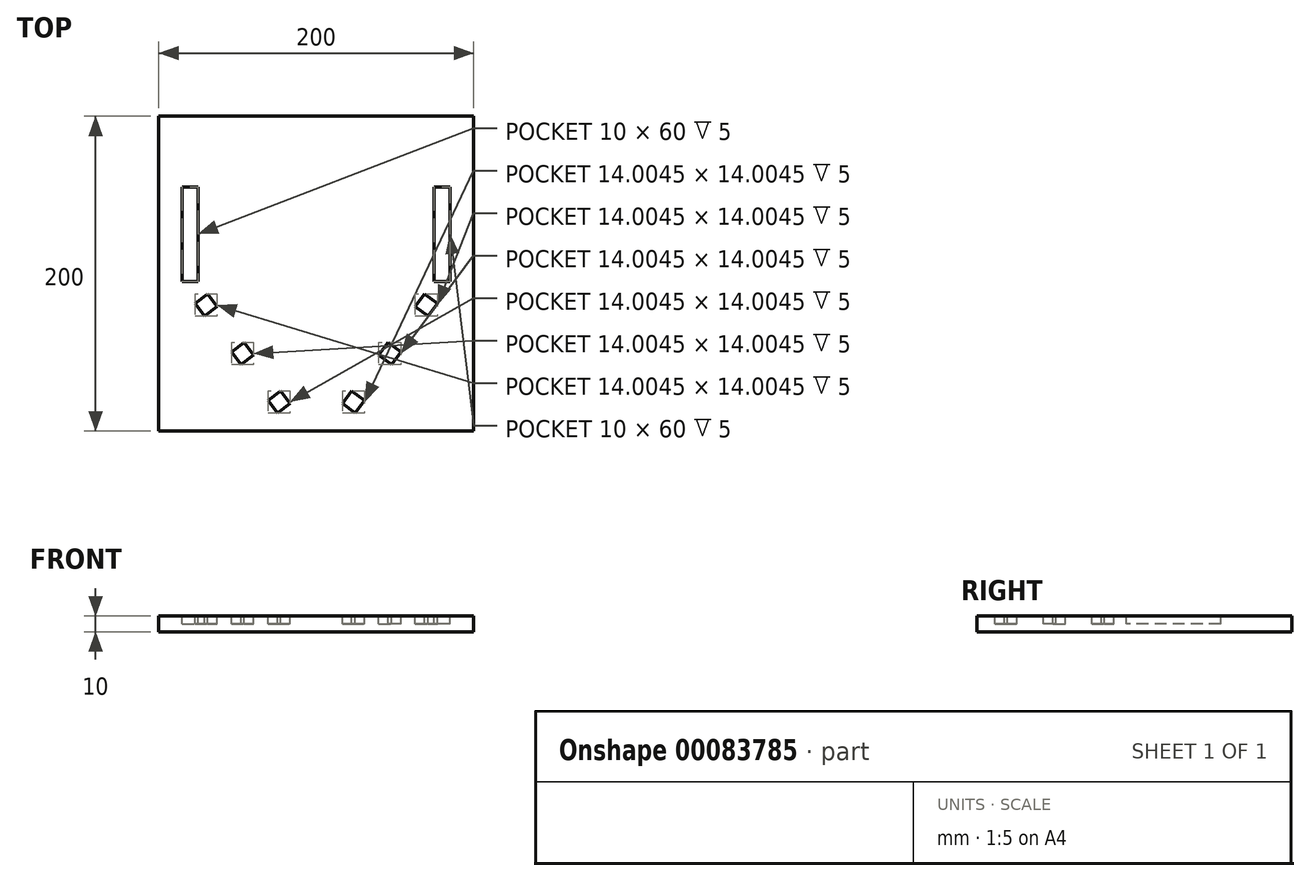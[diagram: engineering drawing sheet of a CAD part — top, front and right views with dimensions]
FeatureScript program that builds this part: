
annotation { "Feature Type Name" : "Feature", "Feature Type Description" : "" }
export const myFeature = defineFeature(function(context is Context, id is Id, definition is map)
    precondition{}
    {
        {
            var Q0;
            Q0=qCreatedBy(makeId("Top.planeOp"),FACE);
            var sketch = newSketch(context, id + "F0", { "sketchPlane" : qUnion([Q0])});
            skLineSegment(sketch, "E0.bottom", {"start": v(-100, 100) * mm, "end": v(100, 100) * mm});
            skLineSegment(sketch, "E0.top", {"start": v(-100, -100) * mm, "end": v(100, -100) * mm});
            skLineSegment(sketch, "E0.left", {"start": v(-100, 100) * mm, "end": v(-100, -100) * mm});
            skLineSegment(sketch, "E0.right", {"start": v(100, 100) * mm, "end": v(100, -100) * mm});
            skPoint(sketch, "E0.middle", {"position": v(0, 0) * mm});
            skSolve(sketch);
        }
        {
            var Q0;
            Q0=makeQuery(id+"F0.imprint","IMPRINT",FACE,{"disambiguationData":[TD([[makeQuery(id+"F0.imprint","IMPRINT",EDGE,{"derivedFrom":sQuery(id+"F0.wireOp",EDGE,"E0.bottom")}),-1.0]])]});
            extrude(context, id + "F1", {"entities" : qUnion([Q0]), "depth" : 10 * mm});
        }
        {
            var Q0;
            Q0=makeQuery(id+"F1.opExtrude","CAP_FACE",FACE,{"disambiguationData":[OSD([sQuery(id+"F0.wireOp",EDGE,"E0.bottom"),sQuery(id+"F0.wireOp",EDGE,"E0.top"),sQuery(id+"F0.wireOp",EDGE,"E0.left"),sQuery(id+"F0.wireOp",EDGE,"E0.right")])],"isStart":false});
            var sketch = newSketch(context, id + "F2", { "sketchPlane" : qUnion([Q0])});
            skLineSegment(sketch, "E1", {"start": v(-100, 25) * mm, "end": v(100, 25) * mm, "construction": true});
            skLineSegment(sketch, "E2.bottom", {"start": v(-85, 55) * mm, "end": v(-75, 55) * mm});
            skLineSegment(sketch, "E2.top", {"start": v(-85, -5) * mm, "end": v(-75, -5) * mm});
            skLineSegment(sketch, "E2.left", {"start": v(-85, 55) * mm, "end": v(-85, -5) * mm});
            skLineSegment(sketch, "E2.right", {"start": v(-75, 55) * mm, "end": v(-75, -5) * mm});
            skPoint(sketch, "E2.middle", {"position": v(-80, 25) * mm});
            skLineSegment(sketch, "E3", {"start": v(0, 100) * mm, "end": v(0, -100) * mm, "construction": true});
            skLineSegment(sketch, "E4.MirrorCS", {"start": v(85, 55) * mm, "end": v(75, 55) * mm});
            skLineSegment(sketch, "E5.MirrorCS", {"start": v(85, -5) * mm, "end": v(75, -5) * mm});
            skLineSegment(sketch, "E6.MirrorCS", {"start": v(75, 55) * mm, "end": v(75, -5) * mm});
            skLineSegment(sketch, "E7.MirrorCS", {"start": v(85, 55) * mm, "end": v(85, -5) * mm});
            skPoint(sketch, "E8.MirrorP", {"position": v(80, 25) * mm});
            skLineSegment(sketch, "E9", {"start": v(-75, -5) * mm, "end": v(-10.6, -90.45) * mm, "construction": true});
            skLineSegment(sketch, "E10", {"start": v(-10.6, -90.45) * mm, "end": v(-18.6, -96.47) * mm, "construction": true});
            skLineSegment(sketch, "E11", {"start": v(-18.6, -96.47) * mm, "end": v(-82.99, -11.02) * mm, "construction": true});
            skLineSegment(sketch, "E12", {"start": v(-82.99, -11.02) * mm, "end": v(-75, -5) * mm, "construction": true});
            skLineSegment(sketch, "E13.MirrorCS", {"start": v(82.99, -11.02) * mm, "end": v(75, -5) * mm, "construction": true});
            skLineSegment(sketch, "E14.MirrorCS", {"start": v(10.6, -90.45) * mm, "end": v(18.6, -96.47) * mm, "construction": true});
            skLineSegment(sketch, "E15.MirrorCS", {"start": v(18.6, -96.47) * mm, "end": v(82.99, -11.02) * mm, "construction": true});
            skLineSegment(sketch, "E16.MirrorCS", {"start": v(75, -5) * mm, "end": v(10.6, -90.45) * mm, "construction": true});
            skLineSegment(sketch, "E17", {"start": v(-76.97, -19) * mm, "end": v(-68.98, -12.99) * mm});
            skLineSegment(sketch, "E18", {"start": v(-68.98, -12.99) * mm, "end": v(-62.96, -20.97) * mm});
            skLineSegment(sketch, "E19", {"start": v(-62.96, -20.97) * mm, "end": v(-70.95, -27) * mm});
            skLineSegment(sketch, "E20", {"start": v(-70.95, -27) * mm, "end": v(-76.97, -19) * mm});
            skLineSegment(sketch, "E21", {"start": v(-42.8, -47.73) * mm, "end": v(-50.79, -53.75) * mm, "construction": true});
            skLineSegment(sketch, "E22", {"start": v(-53.8, -49.75) * mm, "end": v(-45.81, -43.73) * mm});
            skLineSegment(sketch, "E23", {"start": v(-45.81, -43.73) * mm, "end": v(-39.8, -51.72) * mm});
            skLineSegment(sketch, "E24", {"start": v(-39.8, -51.72) * mm, "end": v(-47.78, -57.74) * mm});
            skLineSegment(sketch, "E25", {"start": v(-47.78, -57.74) * mm, "end": v(-53.8, -49.75) * mm});
            skLineSegment(sketch, "E26.MirrorCS", {"start": v(-30.63, -80.5) * mm, "end": v(-24.61, -88.49) * mm});
            skLineSegment(sketch, "E27.MirrorCS", {"start": v(-24.61, -88.49) * mm, "end": v(-16.62, -82.47) * mm});
            skLineSegment(sketch, "E28.MirrorCS", {"start": v(-16.62, -82.47) * mm, "end": v(-22.64, -74.48) * mm});
            skLineSegment(sketch, "E29.MirrorCS", {"start": v(-22.64, -74.48) * mm, "end": v(-30.63, -80.5) * mm});
            skLineSegment(sketch, "E30.MirrorCS", {"start": v(-39.8, -51.72) * mm, "end": v(-45.81, -43.73) * mm});
            skLineSegment(sketch, "E31.MirrorCS", {"start": v(-53.8, -49.75) * mm, "end": v(-47.78, -57.74) * mm});
            skLineSegment(sketch, "E32.MirrorCS", {"start": v(-45.81, -43.73) * mm, "end": v(-53.8, -49.75) * mm});
            skLineSegment(sketch, "E33.MirrorCS", {"start": v(-47.78, -57.74) * mm, "end": v(-39.8, -51.72) * mm});
            skLineSegment(sketch, "E34.MirrorCS", {"start": v(16.62, -82.47) * mm, "end": v(22.64, -74.48) * mm});
            skLineSegment(sketch, "E35.MirrorCS", {"start": v(68.98, -12.99) * mm, "end": v(62.96, -20.97) * mm});
            skLineSegment(sketch, "E36.MirrorCS", {"start": v(70.95, -27) * mm, "end": v(76.97, -19) * mm});
            skLineSegment(sketch, "E37.MirrorCS", {"start": v(53.8, -49.75) * mm, "end": v(47.78, -57.74) * mm});
            skLineSegment(sketch, "E38.MirrorCS", {"start": v(39.8, -51.72) * mm, "end": v(45.81, -43.73) * mm});
            skLineSegment(sketch, "E39.MirrorCS", {"start": v(22.64, -74.48) * mm, "end": v(30.63, -80.5) * mm});
            skLineSegment(sketch, "E40.MirrorCS", {"start": v(53.8, -49.75) * mm, "end": v(45.81, -43.73) * mm});
            skLineSegment(sketch, "E41.MirrorCS", {"start": v(62.96, -20.97) * mm, "end": v(70.95, -27) * mm});
            skLineSegment(sketch, "E42.MirrorCS", {"start": v(30.63, -80.5) * mm, "end": v(24.61, -88.49) * mm});
            skLineSegment(sketch, "E43.MirrorCS", {"start": v(45.81, -43.73) * mm, "end": v(39.8, -51.72) * mm});
            skLineSegment(sketch, "E44.MirrorCS", {"start": v(47.78, -57.74) * mm, "end": v(53.8, -49.75) * mm});
            skLineSegment(sketch, "E45.MirrorCS", {"start": v(76.97, -19) * mm, "end": v(68.98, -12.99) * mm});
            skLineSegment(sketch, "E46.MirrorCS", {"start": v(39.8, -51.72) * mm, "end": v(47.78, -57.74) * mm});
            skLineSegment(sketch, "E47.MirrorCS", {"start": v(24.61, -88.49) * mm, "end": v(16.62, -82.47) * mm});
            skLineSegment(sketch, "E48.MirrorCS", {"start": v(47.78, -57.74) * mm, "end": v(39.8, -51.72) * mm});
            skLineSegment(sketch, "E49.MirrorCS", {"start": v(45.81, -43.73) * mm, "end": v(53.8, -49.75) * mm});
            skLineSegment(sketch, "E50.MirrorCS", {"start": v(42.8, -47.73) * mm, "end": v(50.79, -53.75) * mm, "construction": true});
            skSolve(sketch);
        }
        {
            var Q0;
            Q0 = qSketchRegion(id + "F2", true);
            extrude(context, id + "F3", {"entities" : qUnion([Q0]), "operationType" : NewBodyOperationType.REMOVE, "oppositeDirection" : true, "depth" : 5 * mm});
        }
    });
